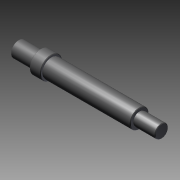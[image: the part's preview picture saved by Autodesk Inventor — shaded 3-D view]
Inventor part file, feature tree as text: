
AUTODESK INVENTOR PART (.ipt)
format: ipt  version: 2011 SP1 (Build 150282100, 282)  size: 153,600 bytes
history: native  units: mm
features: sketch x5, revolve x4, extrude x1
ambient origin geometry x8: Origin, YZ Plane, XZ Plane, XY Plane, X Axis, Y Axis, Z Axis, Center Point
bodies: Solid1 (feature_tree)
feature tree (10):
  revolve  "Revolution1"  Angle=360.0deg
  revolve  "Revolution2"  Angle=360.0deg
  revolve  "Revolution3"  [1 undecoded]
  revolve  "Revolution4"  [1 undecoded]
  extrude  "Extrusion1"  [1 undecoded]
  sketch  "Sketch_1"  dims[d0=360.0deg d1=360.0deg]
  sketch  "Sketch_2"  dims[d2=360.0deg d3=360.0deg]
  sketch  "Sketch_3"  dims[d4=3.0mm d5=0.0mm]
  sketch  "Sketch_4"
  sketch  "Sketch_15"
note: 3 required parameter values undecoded (feature->parameter linkage not recoverable at this tier; creation-order binding heuristic only, values carry confidence <= 0.55)
